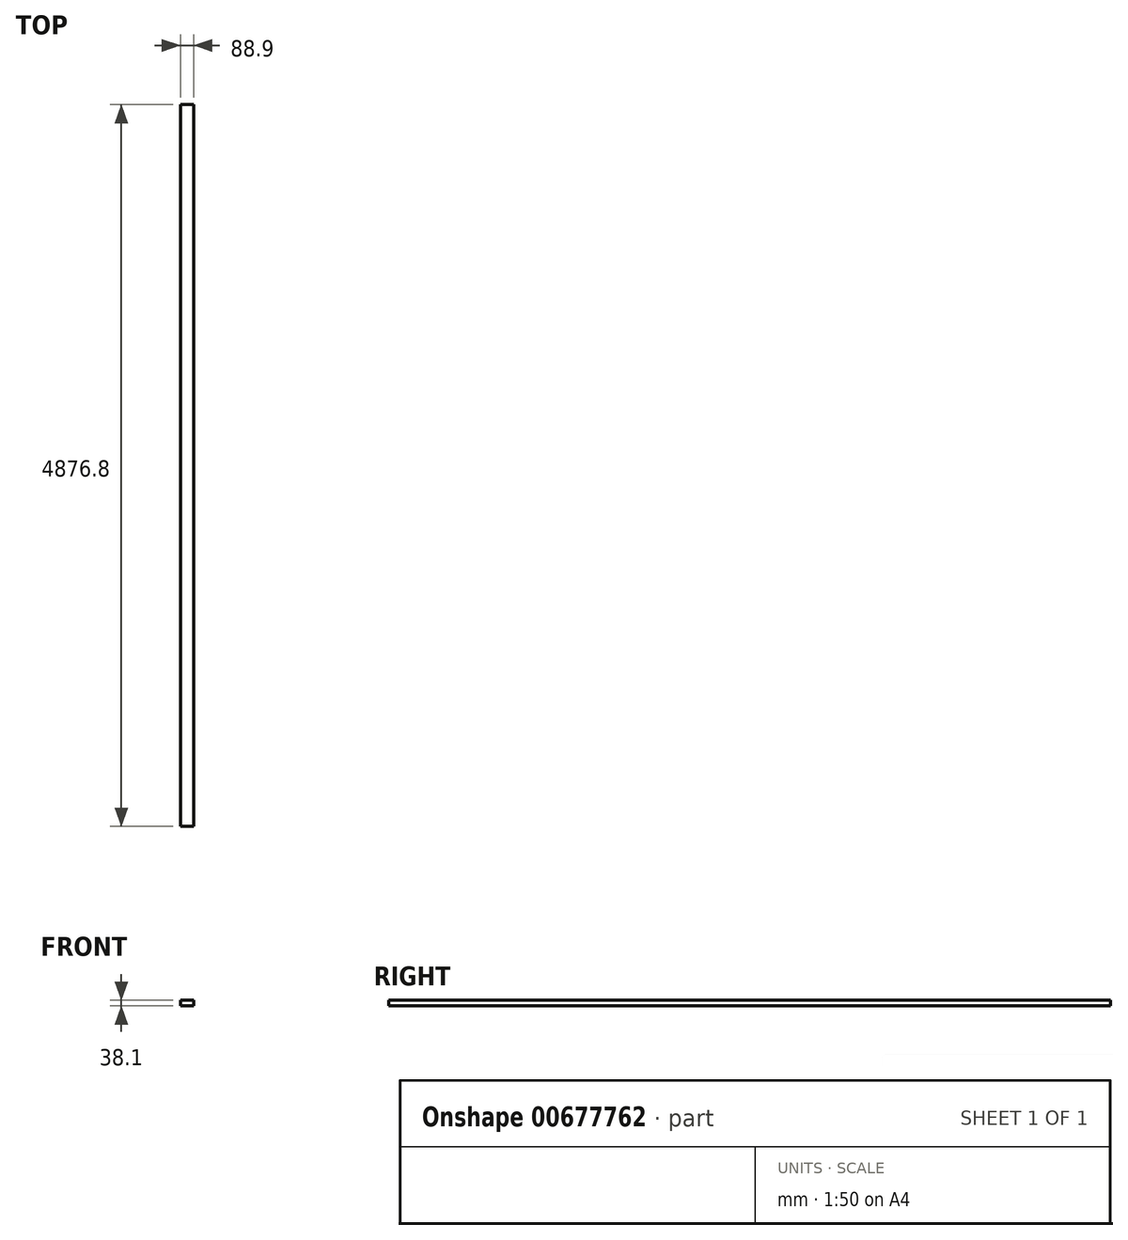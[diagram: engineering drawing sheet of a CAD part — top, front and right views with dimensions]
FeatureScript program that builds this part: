
annotation { "Feature Type Name" : "Feature", "Feature Type Description" : "" }
export const myFeature = defineFeature(function(context is Context, id is Id, definition is map)
    precondition{}
    {
        {
            var Q0;
            Q0=qCreatedBy(makeId("Front.planeOp"),FACE);
            var sketch = newSketch(context, id + "F0", { "sketchPlane" : qUnion([Q0])});
            skLineSegment(sketch, "E0.bottom", {"start": v(212.74, -126.78) * mm, "end": v(301.64, -126.78) * mm});
            skLineSegment(sketch, "E0.top", {"start": v(212.74, -164.88) * mm, "end": v(301.64, -164.88) * mm});
            skLineSegment(sketch, "E0.left", {"start": v(212.74, -126.78) * mm, "end": v(212.74, -164.88) * mm});
            skLineSegment(sketch, "E0.right", {"start": v(301.64, -126.78) * mm, "end": v(301.64, -164.88) * mm});
            skSolve(sketch);
        }
        {
            var Q0;
            Q0=makeQuery(id+"F0.imprint","IMPRINT",FACE,{"disambiguationData":[TD([[makeQuery(id+"F0.imprint","IMPRINT",EDGE,{"derivedFrom":sQuery(id+"F0.wireOp",EDGE,"E0.bottom")}),-1.0]])]});
            extrude(context, id + "F1", {"entities" : qUnion([Q0]), "depth" : 4876.8 * mm, "offsetDistance" : 25.4 * mm});
        }
    });
